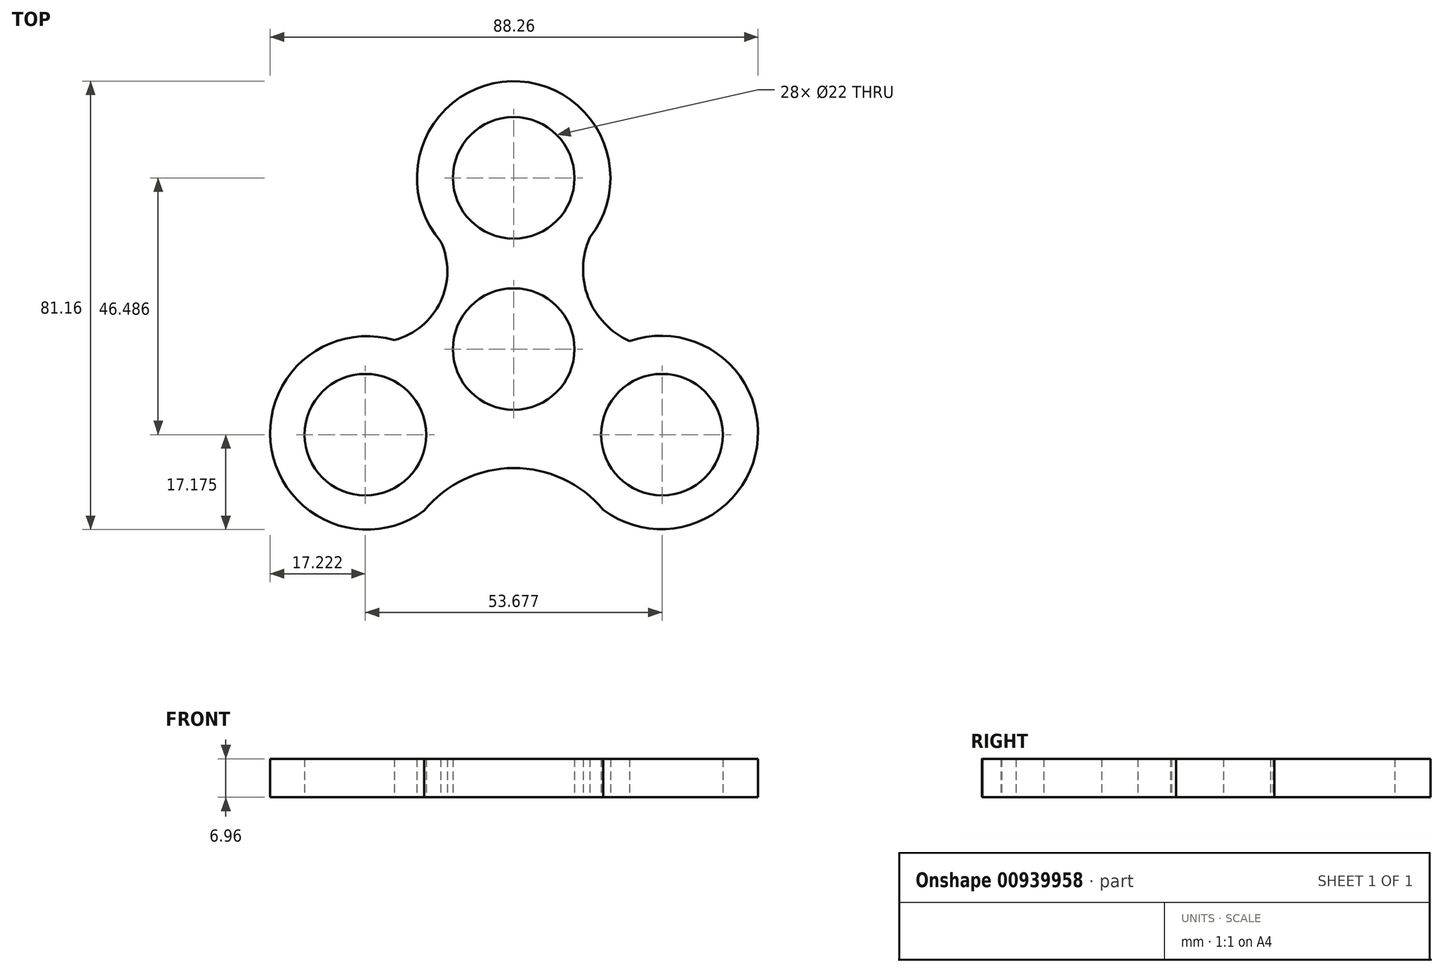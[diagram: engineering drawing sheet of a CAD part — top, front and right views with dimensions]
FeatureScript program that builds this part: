
annotation { "Feature Type Name" : "Feature", "Feature Type Description" : "" }
export const myFeature = defineFeature(function(context is Context, id is Id, definition is map)
    precondition{}
    {
        {
            var Q0;
            Q0=qCreatedBy(makeId("Top.planeOp"),FACE);
            var sketch = newSketch(context, id + "F0", { "sketchPlane" : qUnion([Q0])});
            skCircle(sketch, "E0", {"center": v(0, 0) * mm, "radius": 11 * mm});
            skCircle(sketch, "E1", {"center": v(0, 31) * mm, "radius": 11 * mm});
            skCircle(sketch, "E2.1.0", {"center": v(-26.84, -15.5) * mm, "radius": 11 * mm});
            skCircle(sketch, "E2.2.0", {"center": v(26.84, -15.5) * mm, "radius": 11 * mm});
            skArc(sketch, "E3", {"start": v(13.8, 20.22) * mm, "mid": v(-0.47, 48.48) * mm, "end": v(-13.19, 19.49) * mm});
            skArc(sketch, "E4.1.0", {"start": v(-21.6, 1.61) * mm, "mid": v(-43.22, -20.53) * mm, "end": v(-12.74, -25.91) * mm});
            skArc(sketch, "E4.2.0", {"start": v(13, -25.98) * mm, "mid": v(43.5, -19.97) * mm, "end": v(20.97, 1.45) * mm});
            skPoint(sketch, "E4.center", {"position": v(0.05, 0.24) * mm});
            skArc(sketch, "E5", {"start": v(-21.6, 1.61) * mm, "mid": v(-13.23, 8.6) * mm, "end": v(-13.19, 19.49) * mm});
            skArc(sketch, "E6", {"start": v(13.8, 20.22) * mm, "mid": v(13.48, 9.34) * mm, "end": v(20.97, 1.45) * mm});
            skArc(sketch, "E7", {"start": v(16.22, -29.1) * mm, "mid": v(-0.01, -21.53) * mm, "end": v(-16.17, -29.26) * mm});
            skSolve(sketch);
        }
        {
            var Q0;
            Q0=makeQuery(id+"F0.imprint","IMPRINT",FACE,{"disambiguationData":[TD([[makeQuery(id+"F0.imprint","IMPRINT",EDGE,{"derivedFrom":sQuery(id+"F0.wireOp",EDGE,"E0")}),-1.0]])]});
            extrude(context, id + "F1", {"entities" : qUnion([Q0]), "depth" : 6.96 * mm, "offsetDistance" : 25 * mm});
        }
    });
